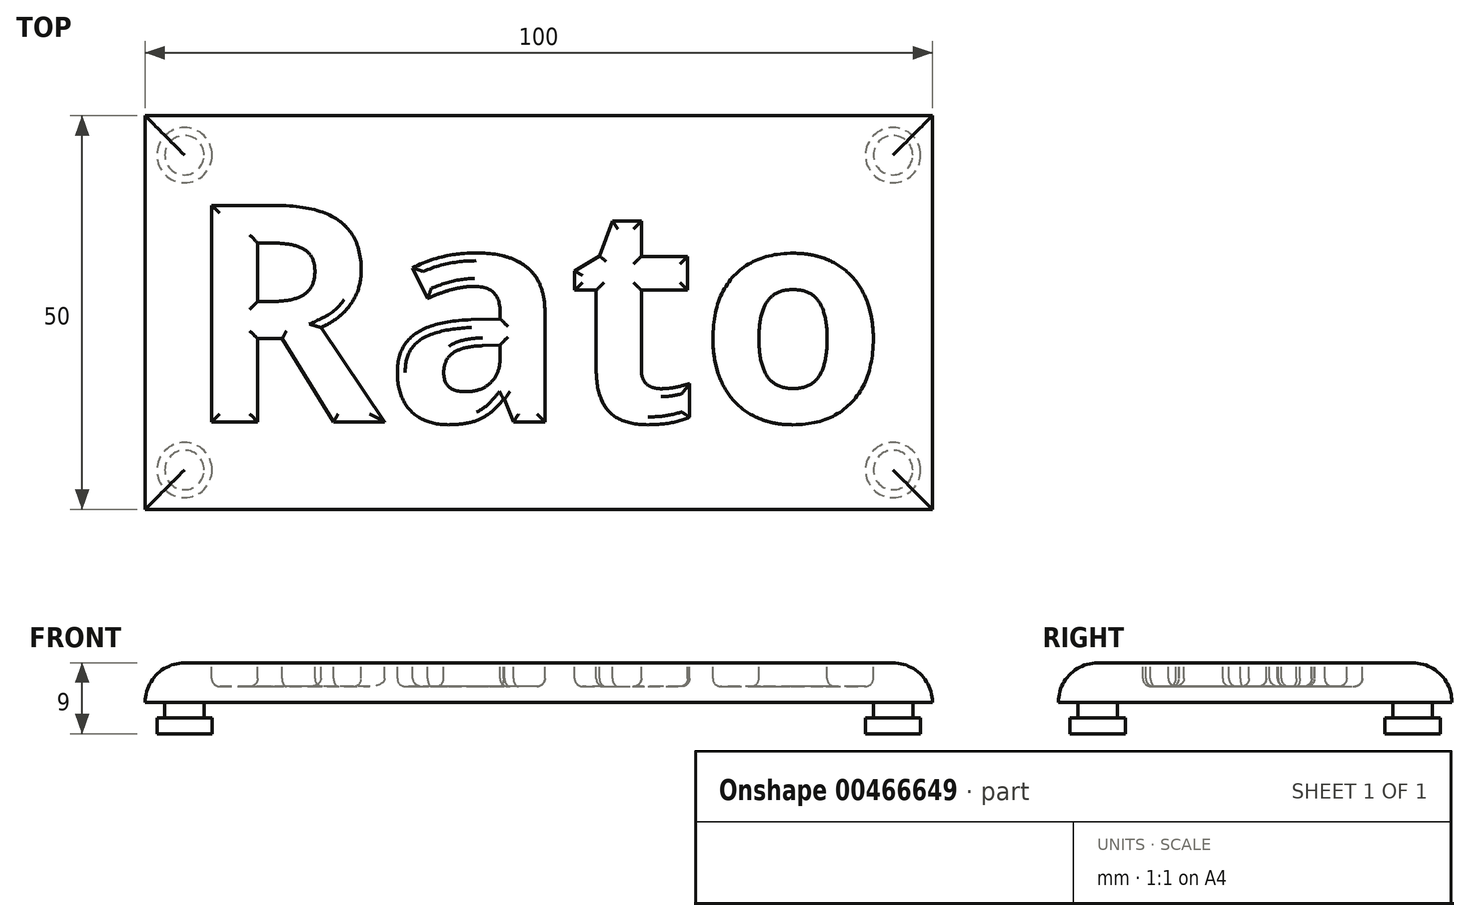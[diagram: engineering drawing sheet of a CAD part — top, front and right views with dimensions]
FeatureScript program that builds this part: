
annotation { "Feature Type Name" : "Feature", "Feature Type Description" : "" }
export const myFeature = defineFeature(function(context is Context, id is Id, definition is map)
    precondition{}
    {
        {
            var Q0;
            Q0=qCreatedBy(makeId("Top.planeOp"),FACE);
            var sketch = newSketch(context, id + "F0", { "sketchPlane" : qUnion([Q0])});
            skLineSegment(sketch, "E0.bottom", {"start": v(50, -25) * mm, "end": v(-50, -25) * mm});
            skLineSegment(sketch, "E0.top", {"start": v(50, 25) * mm, "end": v(-50, 25) * mm});
            skLineSegment(sketch, "E0.left", {"start": v(50, -25) * mm, "end": v(50, 25) * mm});
            skLineSegment(sketch, "E0.right", {"start": v(-50, -25) * mm, "end": v(-50, 25) * mm});
            skPoint(sketch, "E0.middle", {"position": v(0, 0) * mm});
            skSolve(sketch);
        }
        {
            var Q0;
            Q0=qSketchRegion(id+"F0",true);
            extrude(context, id + "F1", {"entities" : qUnion([Q0]), "depth" : 5 * mm});
        }
        {
            var Q0;
            Q0=makeQuery(id+"F1.opExtrude","CAP_EDGE",EDGE,{"disambiguationData":[OSD([sQuery(id+"F0.wireOp",EDGE,"E0.bottom")])],"isStart":false});
            var Q1;
            Q1=makeQuery(id+"F1.opExtrude","CAP_EDGE",EDGE,{"disambiguationData":[OSD([sQuery(id+"F0.wireOp",EDGE,"E0.right")])],"isStart":false});
            var Q2;
            Q2=makeQuery(id+"F1.opExtrude","CAP_EDGE",EDGE,{"disambiguationData":[OSD([sQuery(id+"F0.wireOp",EDGE,"E0.left")])],"isStart":false});
            var Q3;
            Q3=makeQuery(id+"F1.opExtrude","CAP_EDGE",EDGE,{"disambiguationData":[OSD([sQuery(id+"F0.wireOp",EDGE,"E0.top")])],"isStart":false});
            fillet(context, id + "F2", {"entities" : qUnion([Q0, Q1, Q2, Q3]), "radius" : 5 * mm, "tangentPropagation" : true, "allowEdgeOverflow" : false});
        }
        {
            var Q0;
            Q0=makeQuery(id+"F0.imprint","IMPRINT",FACE,{"disambiguationData":[TD([[makeQuery(id+"F0.imprint","IMPRINT",EDGE,{"derivedFrom":sQuery(id+"F0.wireOp",EDGE,"E0.bottom")}),-1.0]])]});
            var sketch = newSketch(context, id + "F3", { "sketchPlane" : qUnion([Q0])});
            skPoint(sketch, "E1.middle", {"position": v(0, 0) * mm});
            skCircle(sketch, "E2", {"center": v(-45, -20) * mm, "radius": 2.5 * mm});
            skCircle(sketch, "E3", {"center": v(45, -20) * mm, "radius": 2.5 * mm});
            skCircle(sketch, "E4", {"center": v(45, 20) * mm, "radius": 2.5 * mm});
            skCircle(sketch, "E5", {"center": v(-45, 20) * mm, "radius": 2.5 * mm});
            skSolve(sketch);
        }
        {
            var Q0;
            Q0=makeQuery(id+"F3.imprint","IMPRINT",FACE,{"disambiguationData":[TD([[makeQuery(id+"F3.imprint","IMPRINT",EDGE,{"derivedFrom":sQuery(id+"F3.wireOp",EDGE,"E2")}),1.0]])]});
            var Q1;
            Q1=makeQuery(id+"F3.imprint","IMPRINT",FACE,{"disambiguationData":[TD([[makeQuery(id+"F3.imprint","IMPRINT",EDGE,{"derivedFrom":sQuery(id+"F3.wireOp",EDGE,"E3")}),1.0]])]});
            var Q2;
            Q2=makeQuery(id+"F3.imprint","IMPRINT",FACE,{"disambiguationData":[TD([[makeQuery(id+"F3.imprint","IMPRINT",EDGE,{"derivedFrom":sQuery(id+"F3.wireOp",EDGE,"E4")}),1.0]])]});
            var Q3;
            Q3=makeQuery(id+"F3.imprint","IMPRINT",FACE,{"disambiguationData":[TD([[makeQuery(id+"F3.imprint","IMPRINT",EDGE,{"derivedFrom":sQuery(id+"F3.wireOp",EDGE,"E5")}),1.0]])]});
            var Q4;
            Q4=qConstructionFilter(qBodyType(qCreatedBy(id+"F3",EDGE),BodyType.WIRE),ConstructionObject.NO);
            extrude(context, id + "F4", {"entities" : qUnion([Q0, Q1, Q2, Q3]), "surfaceEntities" : qUnion([Q4]), "oppositeDirection" : true, "depth" : 2 * mm});
        }
        {
            var Q0;
            Q0=makeQuery(id+"F4.opExtrude","CAP_FACE",FACE,{"disambiguationData":[OSD([sQuery(id+"F3.wireOp",EDGE,"E2")])],"isStart":false});
            var sketch = newSketch(context, id + "F5", { "sketchPlane" : qUnion([Q0])});
            skCircle(sketch, "E6", {"center": v(-45, 20) * mm, "radius": 3.5 * mm});
            skSolve(sketch);
        }
        {
            var Q0;
            Q0=qSketchRegion(id+"F5",true);
            extrude(context, id + "F6", {"entities" : qUnion([Q0]), "operationType" : NewBodyOperationType.ADD, "depth" : 2 * mm});
        }
        {
            var Q0;
            Q0=makeQuery(id+"F4.opExtrude","CAP_FACE",FACE,{"disambiguationData":[OSD([sQuery(id+"F3.wireOp",EDGE,"E3")])],"isStart":false});
            var sketch = newSketch(context, id + "F7", { "sketchPlane" : qUnion([Q0])});
            skCircle(sketch, "E7", {"center": v(45, 20) * mm, "radius": 3.5 * mm});
            skSolve(sketch);
        }
        {
            var Q0;
            Q0=qSketchRegion(id+"F7",true);
            extrude(context, id + "F8", {"entities" : qUnion([Q0]), "operationType" : NewBodyOperationType.ADD, "depth" : 2 * mm});
        }
        {
            var Q0;
            Q0=makeQuery(id+"F4.opExtrude","CAP_FACE",FACE,{"disambiguationData":[OSD([sQuery(id+"F3.wireOp",EDGE,"E5")])],"isStart":false});
            var sketch = newSketch(context, id + "F9", { "sketchPlane" : qUnion([Q0])});
            skCircle(sketch, "E8", {"center": v(-45, -20) * mm, "radius": 3.5 * mm});
            skSolve(sketch);
        }
        {
            var Q0;
            Q0=qSketchRegion(id+"F9",true);
            extrude(context, id + "F10", {"entities" : qUnion([Q0]), "operationType" : NewBodyOperationType.ADD, "depth" : 2 * mm});
        }
        {
            var Q0;
            Q0=makeQuery(id+"F4.opExtrude","CAP_FACE",FACE,{"disambiguationData":[OSD([sQuery(id+"F3.wireOp",EDGE,"E4")])],"isStart":false});
            var sketch = newSketch(context, id + "F11", { "sketchPlane" : qUnion([Q0])});
            skCircle(sketch, "E9", {"center": v(45, -20) * mm, "radius": 3.5 * mm});
            skSolve(sketch);
        }
        {
            var Q0;
            Q0=qSketchRegion(id+"F11",true);
            extrude(context, id + "F12", {"entities" : qUnion([Q0]), "operationType" : NewBodyOperationType.ADD, "depth" : 2 * mm});
        }
        {
            var Q0;
            Q0=makeQuery(id+"F1.opExtrude","CAP_FACE",FACE,{"disambiguationData":[OSD([sQuery(id+"F0.wireOp",EDGE,"E0.bottom"),sQuery(id+"F0.wireOp",EDGE,"E0.top"),sQuery(id+"F0.wireOp",EDGE,"E0.left"),sQuery(id+"F0.wireOp",EDGE,"E0.right")])],"isStart":false});
            var sketch = newSketch(context, id + "F13", { "sketchPlane" : qUnion([Q0])});
            skPoint(sketch, "E10", {"position": v(0, 0) * mm});
            skText(sketch, "E11", { "text": "Rato", "fontName": "NotoSans-Bold.ttf"});
            skLineSegment(sketch, "E12", {"start": v(0, 13.85) * mm, "end": v(0, 0) * mm});
            skLineSegment(sketch, "E13", {"start": v(0, 0) * mm, "end": v(0, -13.87) * mm});
            const initialGuessF13  = {"E11": [-0.045, -0.01387, 1, 0, 0.02772]};
            skSetInitialGuess(sketch, initialGuessF13);
            skSolve(sketch);
        }
        {
            var Q0;
            Q0=qSketchRegion(id+"F13",true);
            extrude(context, id + "F14", {"entities" : qUnion([Q0]), "operationType" : NewBodyOperationType.REMOVE, "oppositeDirection" : true, "depth" : 3 * mm});
        }
        {
            var Q0;
            Q0=makeQuery(id+"F14.boolean.opBoolean","COPY",FACE,{"derivedFrom":makeQuery(id+"F14.opExtrude","CAP_FACE",FACE,{"disambiguationData":[OSD([sQuery(id+"F13.wireOp",EDGE,"E11.sketch_text.stroke-0"),sQuery(id+"F13.wireOp",EDGE,"E11.sketch_text.stroke-1"),sQuery(id+"F13.wireOp",EDGE,"E11.sketch_text.stroke-2"),sQuery(id+"F13.wireOp",EDGE,"E11.sketch_text.stroke-3"),sQuery(id+"F13.wireOp",EDGE,"E11.sketch_text.stroke-4"),sQuery(id+"F13.wireOp",EDGE,"E11.sketch_text.stroke-5"),sQuery(id+"F13.wireOp",EDGE,"E11.sketch_text.stroke-6"),sQuery(id+"F13.wireOp",EDGE,"E11.sketch_text.stroke-7"),sQuery(id+"F13.wireOp",EDGE,"E11.sketch_text.stroke-8"),sQuery(id+"F13.wireOp",EDGE,"E11.sketch_text.stroke-9"),sQuery(id+"F13.wireOp",EDGE,"E11.sketch_text.stroke-10"),sQuery(id+"F13.wireOp",EDGE,"E11.sketch_text.stroke-11"),sQuery(id+"F13.wireOp",EDGE,"E11.sketch_text.stroke-12"),sQuery(id+"F13.wireOp",EDGE,"E11.sketch_text.stroke-13"),sQuery(id+"F13.wireOp",EDGE,"E11.sketch_text.stroke-14"),sQuery(id+"F13.wireOp",EDGE,"E11.sketch_text.stroke-15"),sQuery(id+"F13.wireOp",EDGE,"E11.sketch_text.stroke-16"),sQuery(id+"F13.wireOp",EDGE,"E11.sketch_text.stroke-17"),sQuery(id+"F13.wireOp",EDGE,"E11.sketch_text.stroke-18")])],"isStart":false})});
            var Q1;
            Q1=makeQuery(id+"F14.boolean.opBoolean","COPY",FACE,{"derivedFrom":makeQuery(id+"F14.opExtrude","CAP_FACE",FACE,{"disambiguationData":[OSD([sQuery(id+"F13.wireOp",EDGE,"E11.sketch_text.stroke-19"),sQuery(id+"F13.wireOp",EDGE,"E11.sketch_text.stroke-20"),sQuery(id+"F13.wireOp",EDGE,"E11.sketch_text.stroke-21"),sQuery(id+"F13.wireOp",EDGE,"E11.sketch_text.stroke-22"),sQuery(id+"F13.wireOp",EDGE,"E11.sketch_text.stroke-23"),sQuery(id+"F13.wireOp",EDGE,"E11.sketch_text.stroke-24"),sQuery(id+"F13.wireOp",EDGE,"E11.sketch_text.stroke-25"),sQuery(id+"F13.wireOp",EDGE,"E11.sketch_text.stroke-26"),sQuery(id+"F13.wireOp",EDGE,"E11.sketch_text.stroke-27"),sQuery(id+"F13.wireOp",EDGE,"E11.sketch_text.stroke-28"),sQuery(id+"F13.wireOp",EDGE,"E11.sketch_text.stroke-29"),sQuery(id+"F13.wireOp",EDGE,"E11.sketch_text.stroke-30"),sQuery(id+"F13.wireOp",EDGE,"E11.sketch_text.stroke-31"),sQuery(id+"F13.wireOp",EDGE,"E11.sketch_text.stroke-32"),sQuery(id+"F13.wireOp",EDGE,"E11.sketch_text.stroke-33"),sQuery(id+"F13.wireOp",EDGE,"E11.sketch_text.stroke-34"),sQuery(id+"F13.wireOp",EDGE,"E11.sketch_text.stroke-35"),sQuery(id+"F13.wireOp",EDGE,"E11.sketch_text.stroke-36"),sQuery(id+"F13.wireOp",EDGE,"E11.sketch_text.stroke-37"),sQuery(id+"F13.wireOp",EDGE,"E11.sketch_text.stroke-38"),sQuery(id+"F13.wireOp",EDGE,"E11.sketch_text.stroke-39"),sQuery(id+"F13.wireOp",EDGE,"E11.sketch_text.stroke-40"),sQuery(id+"F13.wireOp",EDGE,"E11.sketch_text.stroke-41"),sQuery(id+"F13.wireOp",EDGE,"E11.sketch_text.stroke-42"),sQuery(id+"F13.wireOp",EDGE,"E11.sketch_text.stroke-43")])],"isStart":false})});
            var Q2;
            Q2=makeQuery(id+"F14.boolean.opBoolean","COPY",FACE,{"derivedFrom":makeQuery(id+"F14.opExtrude","CAP_FACE",FACE,{"disambiguationData":[OSD([sQuery(id+"F13.wireOp",EDGE,"E11.sketch_text.stroke-44"),sQuery(id+"F13.wireOp",EDGE,"E11.sketch_text.stroke-45"),sQuery(id+"F13.wireOp",EDGE,"E11.sketch_text.stroke-46"),sQuery(id+"F13.wireOp",EDGE,"E11.sketch_text.stroke-47"),sQuery(id+"F13.wireOp",EDGE,"E11.sketch_text.stroke-48"),sQuery(id+"F13.wireOp",EDGE,"E11.sketch_text.stroke-49"),sQuery(id+"F13.wireOp",EDGE,"E11.sketch_text.stroke-50"),sQuery(id+"F13.wireOp",EDGE,"E11.sketch_text.stroke-51"),sQuery(id+"F13.wireOp",EDGE,"E11.sketch_text.stroke-52"),sQuery(id+"F13.wireOp",EDGE,"E11.sketch_text.stroke-53"),sQuery(id+"F13.wireOp",EDGE,"E11.sketch_text.stroke-54"),sQuery(id+"F13.wireOp",EDGE,"E11.sketch_text.stroke-55"),sQuery(id+"F13.wireOp",EDGE,"E11.sketch_text.stroke-56"),sQuery(id+"F13.wireOp",EDGE,"E11.sketch_text.stroke-57"),sQuery(id+"F13.wireOp",EDGE,"E11.sketch_text.stroke-58"),sQuery(id+"F13.wireOp",EDGE,"E11.sketch_text.stroke-59"),sQuery(id+"F13.wireOp",EDGE,"E11.sketch_text.stroke-60"),sQuery(id+"F13.wireOp",EDGE,"E11.sketch_text.stroke-61")])],"isStart":false})});
            var Q3;
            Q3=makeQuery(id+"F14.boolean.opBoolean","COPY",FACE,{"derivedFrom":makeQuery(id+"F14.opExtrude","CAP_FACE",FACE,{"disambiguationData":[OSD([sQuery(id+"F13.wireOp",EDGE,"E11.sketch_text.stroke-62"),sQuery(id+"F13.wireOp",EDGE,"E11.sketch_text.stroke-63"),sQuery(id+"F13.wireOp",EDGE,"E11.sketch_text.stroke-64"),sQuery(id+"F13.wireOp",EDGE,"E11.sketch_text.stroke-65"),sQuery(id+"F13.wireOp",EDGE,"E11.sketch_text.stroke-66"),sQuery(id+"F13.wireOp",EDGE,"E11.sketch_text.stroke-67"),sQuery(id+"F13.wireOp",EDGE,"E11.sketch_text.stroke-68"),sQuery(id+"F13.wireOp",EDGE,"E11.sketch_text.stroke-69"),sQuery(id+"F13.wireOp",EDGE,"E11.sketch_text.stroke-70"),sQuery(id+"F13.wireOp",EDGE,"E11.sketch_text.stroke-71"),sQuery(id+"F13.wireOp",EDGE,"E11.sketch_text.stroke-72"),sQuery(id+"F13.wireOp",EDGE,"E11.sketch_text.stroke-73"),sQuery(id+"F13.wireOp",EDGE,"E11.sketch_text.stroke-74"),sQuery(id+"F13.wireOp",EDGE,"E11.sketch_text.stroke-75"),sQuery(id+"F13.wireOp",EDGE,"E11.sketch_text.stroke-76"),sQuery(id+"F13.wireOp",EDGE,"E11.sketch_text.stroke-77"),sQuery(id+"F13.wireOp",EDGE,"E11.sketch_text.stroke-78"),sQuery(id+"F13.wireOp",EDGE,"E11.sketch_text.stroke-79")])],"isStart":false})});
            fillet(context, id + "F15", {"entities" : qUnion([Q0, Q1, Q2, Q3]), "radius" : 1 * mm, "tangentPropagation" : true, "allowEdgeOverflow" : false});
        }
    });
